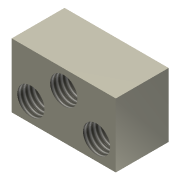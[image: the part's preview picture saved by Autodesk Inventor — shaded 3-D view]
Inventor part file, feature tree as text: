
AUTODESK INVENTOR PART (.ipt)
format: ipt  version: 2011 (Build 150239000, 239)  size: 111,104 bytes
history: native  units: in
note: dims shown in document units (in); Inventor stores cm internally (conversion verified against a paired STEP export)
features: thread x5, extrude x3, sketch x3
ambient origin geometry x8: Origin, YZ Plane, XZ Plane, XY Plane, X Axis, Y Axis, Z Axis, Center Point
bodies: Solid1 (feature_tree)
feature tree (11):
  extrude  "Extrusion1"  Depth=1.0in
  extrude  "Extrusion2"  Depth=0.425in
  thread  "Thread1"  [1 undecoded]
  thread  "Thread2"  [1 undecoded]
  thread  "Thread3"  [1 undecoded]
  extrude  "Extrusion3"  Depth=0.3in
  thread  "Thread4"  [1 undecoded]
  thread  "Thread5"  [1 undecoded]
  sketch  "Sketch1"  dims[d0=1.625in d1=1.0in]
  sketch  "Sketch2"  dims[d2=0.825in d3=0.0in d4=0.425in d5=0.3in d6=0.3in d7=0.3in]
  sketch  "Sketch3"  dims[d8=0.3in d9=0.3in d10=0.375in d11=0.0in d12=1.0in d13=0.0in d14=1.0in d15=0.0in d16=1.0in d17=0.0in d18=0.425in d19=0.75in d20=0.4375in d21=0.375in d22=0.0in d23=1.0in d24=0.0in d25=1.0in d26=0.0in]
note: 5 required parameter values undecoded (feature->parameter linkage not recoverable at this tier; creation-order binding heuristic only, values carry confidence <= 0.55)
